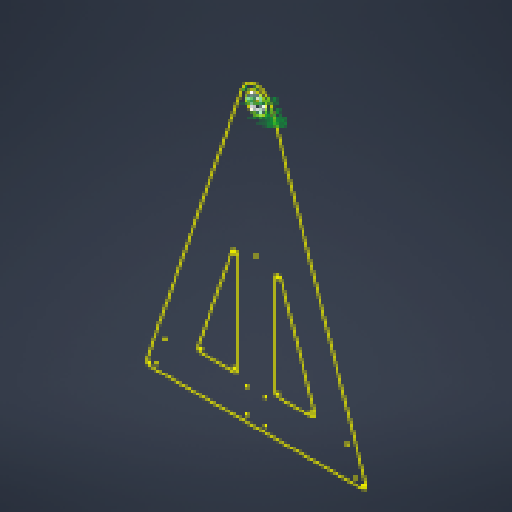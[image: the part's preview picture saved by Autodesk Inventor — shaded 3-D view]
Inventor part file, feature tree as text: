
AUTODESK INVENTOR PART (.ipt)
format: ipt  version: 2024.1 (Build 281209000, 209)  size: 179,712 bytes
history: native  units: in
note: dims shown in document units (in); Inventor stores cm internally (conversion verified against a paired STEP export)
features: other x5, reference x3, extrude x2, sketch x1, chamfer x1
ambient origin geometry x8: Origin, YZ Plane, XZ Plane, XY Plane, X Axis, Y Axis, Z Axis, Center Point
bodies: Solid1 (feature_tree)
feature tree (12):
  sketch  "Sketch1"  dims[d0=0.003in d1=0.1654in d2=0.1654in d3=0.1654in d4=0.1654in d5=0.1654in d6=0.1654in d7=0.2762in d8=0.0in d9=0.3425in d10=0.1762in d11=0.0in d12=0.025in d13=0.125in d14=45.0deg]
  extrude  "Extrusion1"  Depth=0.1762in
  extrude  "Extrusion2"  Depth=0.1762in
  chamfer  "Chamfer1"  Distance=0.1654in
  reference  "Reference1"
  reference  "Reference2"
  reference  "Reference3"
  other  "<userpath>\Documents\School\FallCAD\Trebuchet\Trebuchet.iam"
  other  "Trebuchet.iam"
  other  "MainInnerBearingMount:1"
  other  "FrameTop:1"
  other  "FrameTop:3"
